# Revit family: 18-70-003 DN100
name_source: partatom
category: Pipe Accessories
units: mm (PartAtom-declared; Revit-internal decimal feet)

## family parameters
Always vertical = Yes
Cut with Voids When Loaded = No
Part Type = Valve - Breaks Into
Round Connector Dimension = Use Diameter
Shared = No
Work Plane-Based = No

## types (1)
- DN100_PN10/16
    1 = 1 mm  [stored 0.00328084 ft]
    20 = 20 mm  [stored 0.0656168 ft]
    27 = 27 mm  [stored 0.0885827 ft]
    5 = 5 mm  [stored 0.0164042 ft]
    50 = 50 mm  [stored 0.164042 ft]
    Body_H = 122 mm  [stored 0.400262 ft]
    Bore_R = 50 mm  [stored 0.164042 ft]
    DN = 100 mm  [stored 0.328084 ft]
    DN100_PN10/16 = 18-100-70-0140000099
    Default Elevation = 0 mm  [stored 0 ft]
    Description_ = AVK COMBI-CROSS, FLANGED, 4 OUTLETS, PN10/16
    Dh = 180 mm  [stored 0.590551 ft]
    F = 10 mm  [stored 0.0328084 ft]
    F1 = 12 mm  [stored 0.0393701 ft]
    F2 = 47 mm  [stored 0.154199 ft]
    F3 = 35 mm  [stored 0.114829 ft]
    FL_R = 110 mm  [stored 0.360892 ft]
    FL_T = 18 mm  [stored 0.0590551 ft]
    H = 305 mm  [stored 1.00066 ft]
    H1 = 225 mm  [stored 0.738189 ft]
    H3 = 415 mm  [stored 1.36155 ft]
    H3-H = 110 mm  [stored 0.360892 ft]
    L = 580 mm  [stored 1.90289 ft]
    L-L1 = 120 mm  [stored 0.393701 ft]
    L1 = 340 mm  [stored 1.11549 ft]
    L2 = 106 mm  [stored 0.347769 ft]
    L5 = 143 mm  [stored 0.46916 ft]
    L_half = 145 mm  [stored 0.475722 ft]
    OD = 110 mm  [stored 0.360892 ft]
    OD1 = 61 mm  [stored 0.200131 ft]
    OD2 = 67 mm
    P1 = 240 mm  [stored 0.787402 ft]
    Raised_R = 77 mm
    Raised_dis = 3 mm  [stored 0.00984252 ft]
    Search_table = 18-70-003 DN100
    URL_product_pages = https://www.avkvalves.com
    W = 106 mm  [stored 0.347769 ft]
    body_dim1 = 99 mm
    main_dim1 = 63 mm

note: [stored X ft] marks values corroborated as IEEE doubles in the binary element streams (Revit-internal decimal feet)

## geometry (parser evidence)
native form markers: Sweep x6
no freeform markers — native parametric forms only
